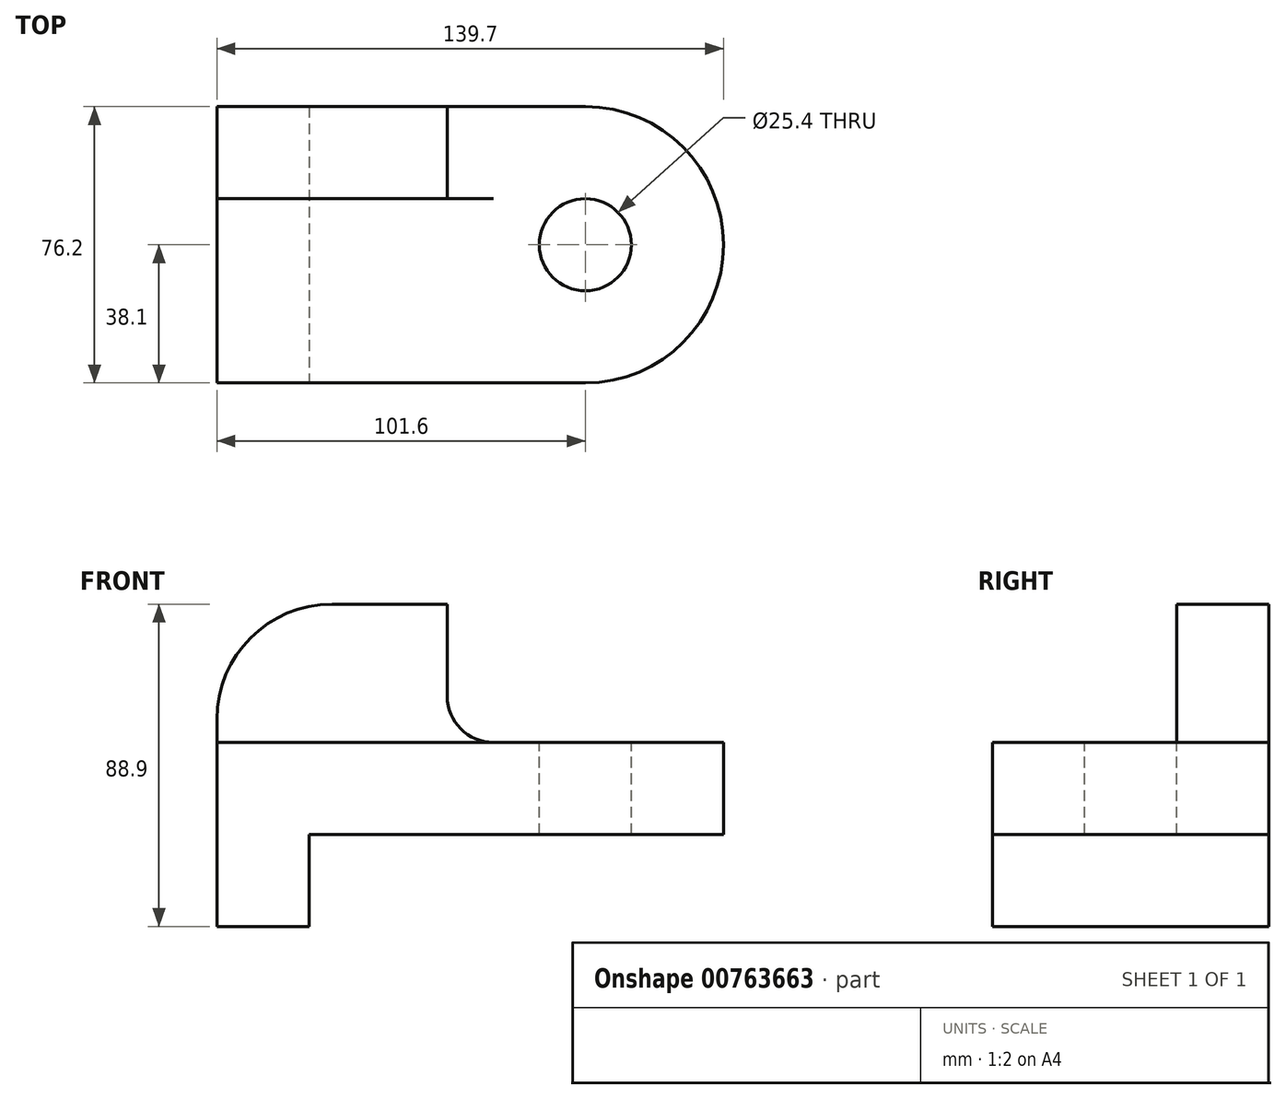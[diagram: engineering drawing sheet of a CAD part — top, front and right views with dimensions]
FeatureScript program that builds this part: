
annotation { "Feature Type Name" : "Feature", "Feature Type Description" : "" }
export const myFeature = defineFeature(function(context is Context, id is Id, definition is map)
    precondition{}
    {
        {
            var Q0;
            Q0=qCreatedBy(makeId("Front.planeOp"),FACE);
            var sketch = newSketch(context, id + "F0", { "sketchPlane" : qUnion([Q0])});
            skLineSegment(sketch, "E0.bottom", {"start": v(69.85, -44.45) * mm, "end": v(-69.85, -44.45) * mm});
            skLineSegment(sketch, "E0.top", {"start": v(69.85, 44.45) * mm, "end": v(-69.85, 44.45) * mm});
            skLineSegment(sketch, "E0.left", {"start": v(69.85, -44.45) * mm, "end": v(69.85, 44.45) * mm});
            skLineSegment(sketch, "E0.right", {"start": v(-69.85, -44.45) * mm, "end": v(-69.85, 44.45) * mm});
            skPoint(sketch, "E0.middle", {"position": v(0, 0) * mm});
            skSolve(sketch);
        }
        {
            var Q0;
            Q0 = qSketchRegion(id + "F0", true);
            extrude(context, id + "F1", {"entities" : qUnion([Q0]), "depth" : 76.2 * mm, "offsetDistance" : 25.4 * mm});
        }
        {
            var Q0;
            Q0=makeQuery(id+"F1.opExtrude","CAP_FACE",FACE,{"disambiguationData":[OSD([sQuery(id+"F0.wireOp",EDGE,"E0.bottom"),sQuery(id+"F0.wireOp",EDGE,"E0.top"),sQuery(id+"F0.wireOp",EDGE,"E0.left"),sQuery(id+"F0.wireOp",EDGE,"E0.right")])],"isStart":false});
            var sketch = newSketch(context, id + "F2", { "sketchPlane" : qUnion([Q0])});
            skLineSegment(sketch, "E1.bottom", {"start": v(-6.35, 44.45) * mm, "end": v(69.85, 44.45) * mm});
            skLineSegment(sketch, "E1.top", {"start": v(-6.35, 6.35) * mm, "end": v(69.85, 6.35) * mm});
            skLineSegment(sketch, "E1.left", {"start": v(-6.35, 44.45) * mm, "end": v(-6.35, 6.35) * mm});
            skLineSegment(sketch, "E1.right", {"start": v(69.85, 44.45) * mm, "end": v(69.85, 6.35) * mm});
            skSolve(sketch);
        }
        {
            var Q0;
            Q0 = qSketchRegion(id + "F2", true);
            extrude(context, id + "F3", {"entities" : qUnion([Q0]), "operationType" : NewBodyOperationType.REMOVE, "oppositeDirection" : true, "depth" : 76.2 * mm, "offsetDistance" : 25.4 * mm});
        }
        {
            var Q0;
            Q0=makeQuery(id+"F1.opExtrude","CAP_FACE",FACE,{"disambiguationData":[OSD([sQuery(id+"F0.wireOp",EDGE,"E0.bottom"),sQuery(id+"F0.wireOp",EDGE,"E0.top"),sQuery(id+"F0.wireOp",EDGE,"E0.left"),sQuery(id+"F0.wireOp",EDGE,"E0.right")])],"isStart":false});
            var sketch = newSketch(context, id + "F4", { "sketchPlane" : qUnion([Q0])});
            skLineSegment(sketch, "E2.bottom", {"start": v(-44.45, -44.45) * mm, "end": v(69.85, -44.45) * mm});
            skLineSegment(sketch, "E2.top", {"start": v(-44.45, -19.05) * mm, "end": v(69.85, -19.05) * mm});
            skLineSegment(sketch, "E2.left", {"start": v(-44.45, -44.45) * mm, "end": v(-44.45, -19.05) * mm});
            skLineSegment(sketch, "E2.right", {"start": v(69.85, -44.45) * mm, "end": v(69.85, -19.05) * mm});
            skSolve(sketch);
        }
        {
            var Q0;
            Q0 = qSketchRegion(id + "F4", true);
            extrude(context, id + "F5", {"entities" : qUnion([Q0]), "operationType" : NewBodyOperationType.REMOVE, "oppositeDirection" : true, "depth" : 76.2 * mm, "offsetDistance" : 25.4 * mm});
        }
        {
            var Q0;
            Q0=makeQuery(id+"F1.opExtrude","SWEPT_FACE",FACE,{"disambiguationData":[OSD([sQuery(id+"F0.wireOp",EDGE,"E0.top")])]});
            var sketch = newSketch(context, id + "F6", { "sketchPlane" : qUnion([Q0])});
            skLineSegment(sketch, "E3.bottom", {"start": v(-69.85, -25.4) * mm, "end": v(-6.35, -25.4) * mm});
            skLineSegment(sketch, "E3.top", {"start": v(-69.85, -76.2) * mm, "end": v(-6.35, -76.2) * mm});
            skLineSegment(sketch, "E3.left", {"start": v(-69.85, -25.4) * mm, "end": v(-69.85, -76.2) * mm});
            skLineSegment(sketch, "E3.right", {"start": v(-6.35, -25.4) * mm, "end": v(-6.35, -76.2) * mm});
            skSolve(sketch);
        }
        {
            var Q0;
            Q0 = qSketchRegion(id + "F6", true);
            extrude(context, id + "F7", {"entities" : qUnion([Q0]), "operationType" : NewBodyOperationType.REMOVE, "oppositeDirection" : true, "depth" : 38.1 * mm, "offsetDistance" : 25.4 * mm});
        }
        {
            var Q0;
            Q0=makeQuery(id+"F1.opExtrude","SWEPT_EDGE",EDGE,{"disambiguationData":[OSD([sQuery(id+"F0.wireOp",EDGE,"E0.top"),sQuery(id+"F0.wireOp",EDGE,"E0.right")])]});
            var Q1;
            Q1=makeQuery(id+"F3.boolean.opBoolean","COPY",EDGE,{"derivedFrom":makeQuery(id+"F3.opExtrude","SWEPT_EDGE",EDGE,{"disambiguationData":[OSD([sQuery(id+"F0.wireOp",EDGE,"E0.top"),sQuery(id+"F2.wireOp",EDGE,"E1.bottom"),sQuery(id+"F2.wireOp",EDGE,"E1.left")])]})});
            fillet(context, id + "F8", {"entities" : qUnion([Q0, Q1]), "radius" : 31.75 * mm, "tangentPropagation" : true, "allowEdgeOverflow" : false});
        }
        {
            var Q0;
            Q0=makeQuery(id+"F1.opExtrude","CAP_EDGE",EDGE,{"disambiguationData":[OSD([sQuery(id+"F0.wireOp",EDGE,"E0.left")])],"isStart":false});
            var Q1;
            Q1=makeQuery(id+"F1.opExtrude","CAP_EDGE",EDGE,{"disambiguationData":[OSD([sQuery(id+"F0.wireOp",EDGE,"E0.left")])],"isStart":true});
            fillet(context, id + "F9", {"entities" : qUnion([Q0, Q1]), "radius" : 38.1 * mm, "tangentPropagation" : true, "allowEdgeOverflow" : false});
        }
        {
            var Q0;
            Q0=makeQuery(id+"F3.boolean.opBoolean","COPY",EDGE,{"derivedFrom":makeQuery(id+"F3.opExtrude","SWEPT_EDGE",EDGE,{"disambiguationData":[OSD([sQuery(id+"F2.wireOp",EDGE,"E1.top"),sQuery(id+"F2.wireOp",EDGE,"E1.left")])]})});
            fillet(context, id + "F10", {"entities" : qUnion([Q0]), "radius" : 12.7 * mm, "tangentPropagation" : true, "allowEdgeOverflow" : false});
        }
        {
            var Q0;
            Q0=makeQuery(id+"F7.boolean.opBoolean","MERGE",FACE,{"derivedFrom":[makeQuery(id+"F3.boolean.opBoolean","COPY",FACE,{"derivedFrom":makeQuery(id+"F3.opExtrude","SWEPT_FACE",FACE,{"disambiguationData":[OSD([sQuery(id+"F2.wireOp",EDGE,"E1.top")])]})}),makeQuery(id+"F7.opExtrude","CAP_FACE",FACE,{"disambiguationData":[OSD([sQuery(id+"F6.wireOp",EDGE,"E3.bottom"),sQuery(id+"F6.wireOp",EDGE,"E3.top"),sQuery(id+"F6.wireOp",EDGE,"E3.left"),sQuery(id+"F6.wireOp",EDGE,"E3.right")])],"isStart":false})]});
            var sketch = newSketch(context, id + "F11", { "sketchPlane" : qUnion([Q0])});
            skCircle(sketch, "E4", {"center": v(31.75, -38.1) * mm, "radius": 12.7 * mm});
            skSolve(sketch);
        }
        {
            var Q0;
            Q0 = qSketchRegion(id + "F11", true);
            extrude(context, id + "F12", {"entities" : qUnion([Q0]), "operationType" : NewBodyOperationType.REMOVE, "oppositeDirection" : true, "depth" : 25.4 * mm, "offsetDistance" : 25.4 * mm});
        }
    });
